# Revit family: Sink-American_Standard-Delancey-77SB16180.308
name_source: partatom
category: Plumbing Fixtures
units: mm (PartAtom-declared; Revit-internal decimal feet)

## family parameters
Always vertical = No
Cut with Voids When Loaded = Yes
OmniClass Number = 23.45.05.14.14
OmniClass Title = Sinks/Lavatories
Part Type = Normal
Room Calculation Point = No
Round Connector Dimension = Use Diameter
Shared = Yes
Work Plane-Based = Yes

## types (1)
- 77SB16180.308
    ASME A112.19.2/CSA B45.1 = Yes
    Assembly Code = D2010410
    Basin Shape = Rectangular
    CW Connection = Yes
    CWFU = 2
    Cold Water Connection Diameter = 1/2"
    Cold Water Connection Height = 10 1/16"
    Cold Water Connection Radius = 1/4"
    Cold Water Connection Width = 4"
    Default Elevation = 34"
    Description = Delancey Single Bowl Kitchen Sink
    Finish = Cast Iron-American Standard-308-Brilliant White
    HW Connection = Yes
    HWFU = 2
    Height = 8"
    Hot Water Connection Diameter = 1"
    Hot Water Connection Height = 10 1/16"
    Hot Water Connection Radius = 1/4"
    Hot Water Connection Width = 4"
    Installation Type = Undermount
    Length = 16"
    Manufacturer = American Standard
    Material = Cast Iron-American Standard-308-Brilliant White
    Model = 77SB16180.308
    Price = Prices may vary. Please consult Manufacturer Representative for most up-to-date price list.
    Product Documentation Link = https://americanstandard.box.com
    Product Page URL = https://www.americanstandard-us.com
    Revised Date = 03/07/2022
    Stainless Steel Bottom Grid 8422000.075 = No
    Stainless Steel Waste Fitting 9028000.075 = No
    Type Comments = Minimum 21" (533mm) cabinet required
    URL = https://www.americanstandard-us.com
    Vent Connection = No
    WFU = 3
    Warranty Information = Limited Lifetime Warranty
    Waste Connection = Yes
    Waste Connection Diameter = 1 1/2"
    Waste Connection Height = 11 9/16"
    Waste Connection Radius = 3/4"
    Width = 18"

## geometry (parser evidence)
native form markers: Sweep x2
no freeform markers — native parametric forms only
